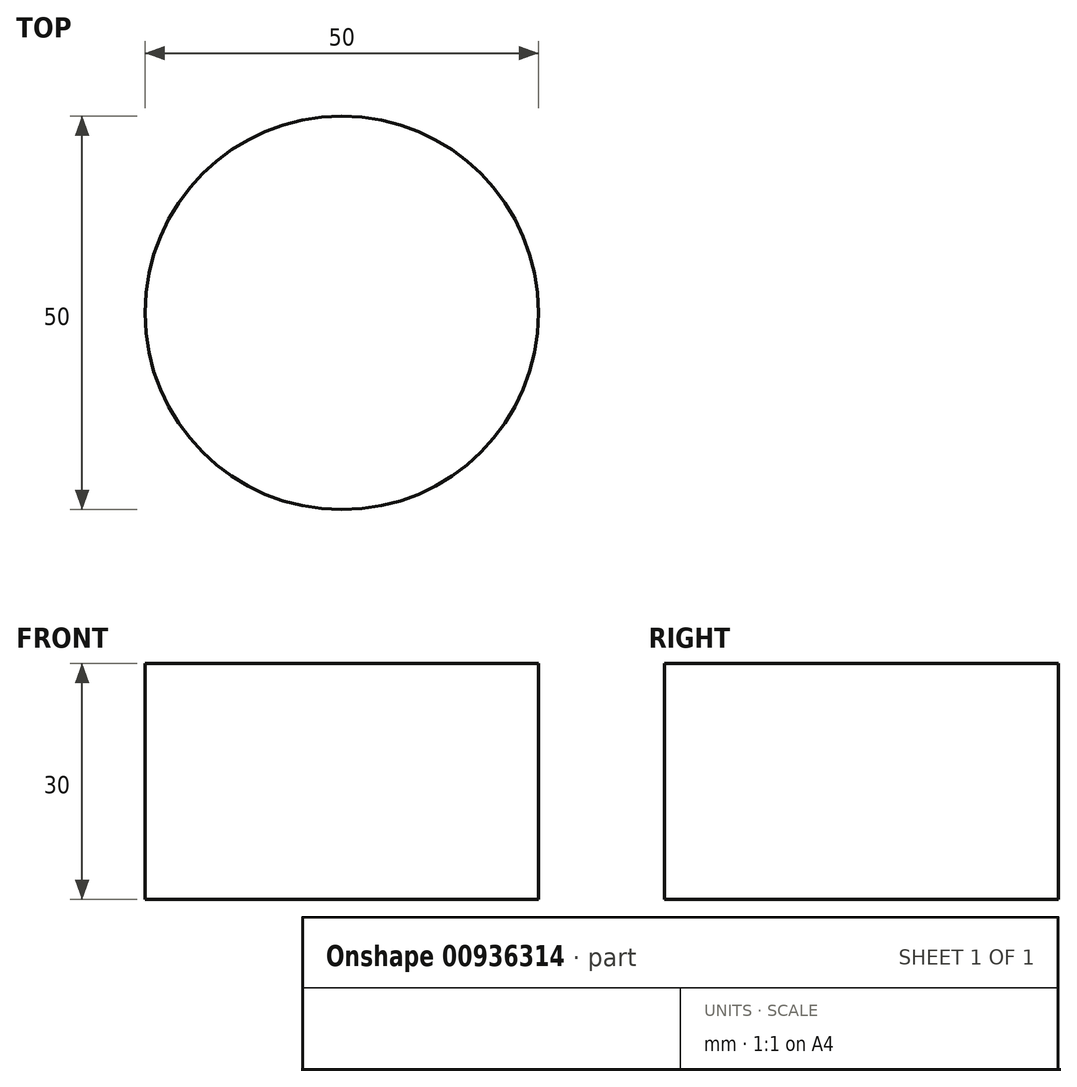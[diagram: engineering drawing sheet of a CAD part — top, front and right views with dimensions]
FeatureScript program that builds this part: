
annotation { "Feature Type Name" : "Feature", "Feature Type Description" : "" }
export const myFeature = defineFeature(function(context is Context, id is Id, definition is map)
    precondition{}
    {
        {
            var Q0;
            Q0=qCreatedBy(makeId("Right.planeOp"),FACE);
            var sketch = newSketch(context, id + "F0", { "sketchPlane" : qUnion([Q0])});
            skLineSegment(sketch, "E0.bottom", {"start": v(0, 0) * mm, "end": v(25, 0) * mm});
            skLineSegment(sketch, "E0.top", {"start": v(0, 30) * mm, "end": v(25, 30) * mm});
            skLineSegment(sketch, "E0.left", {"start": v(0, 0) * mm, "end": v(0, 30) * mm});
            skLineSegment(sketch, "E0.right", {"start": v(25, 0) * mm, "end": v(25, 30) * mm});
            skSolve(sketch);
        }
        {
            var Q0;
            Q0 = qSketchRegion(id + "F0", true);
            var Q1;
            Q1=sQuery(id+"F0.wireOp",EDGE,"E0.left");
            revolve(context, id + "F1", {"surfaceOperationType" : NewSurfaceOperationType.NEW, "entities" : qUnion([Q0]), "axis" : qUnion([Q1]), "revolveType" : RevolveType.FULL});
        }
    });
